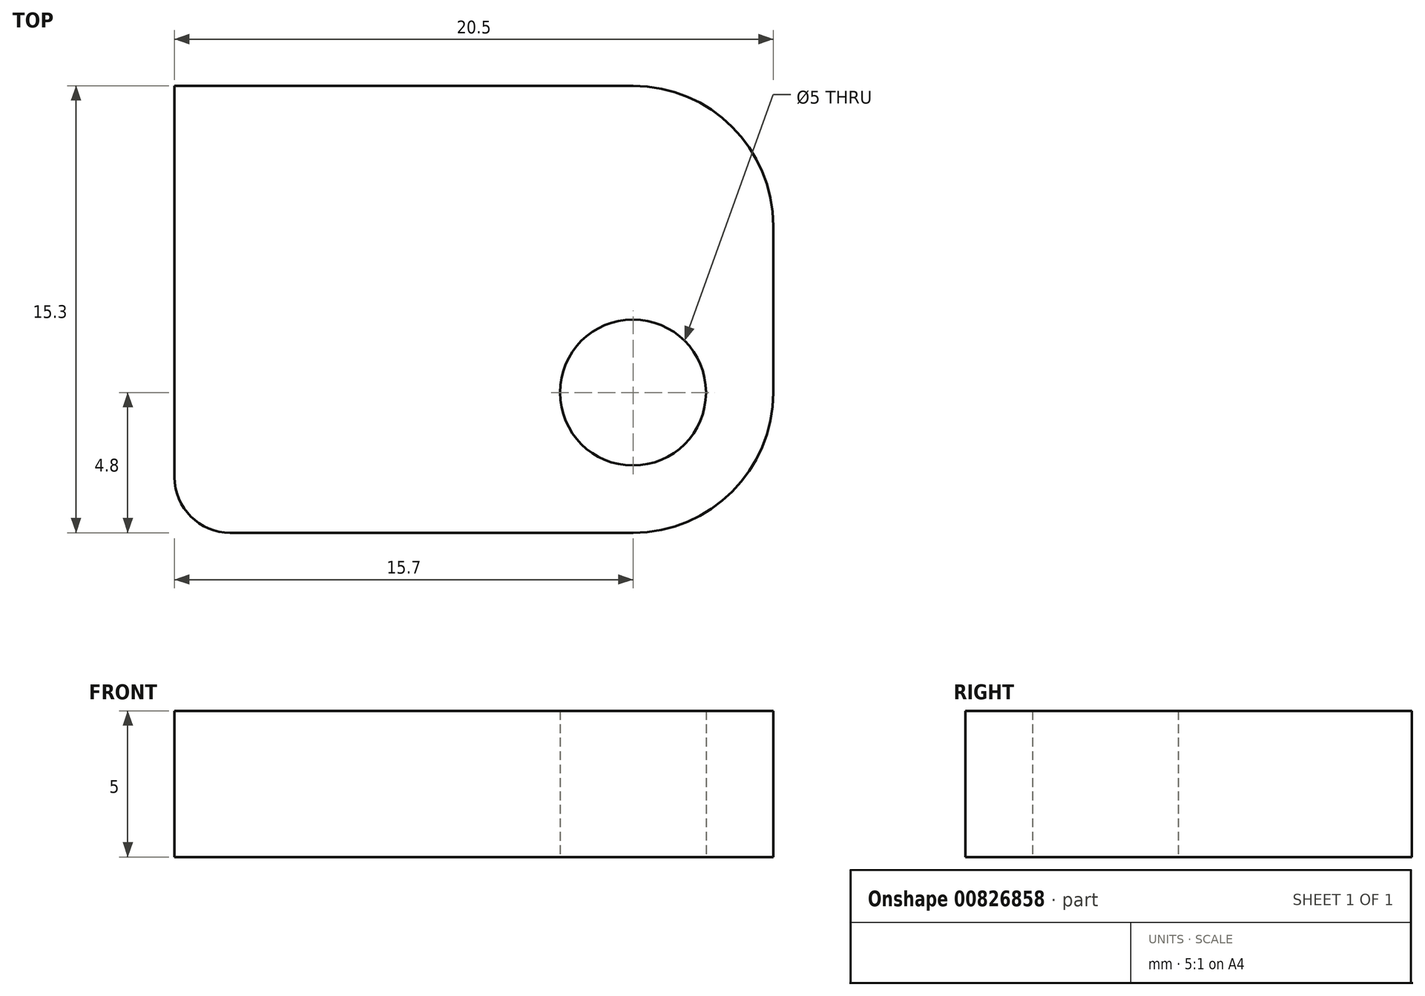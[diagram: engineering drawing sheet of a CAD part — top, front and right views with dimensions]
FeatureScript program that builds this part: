
annotation { "Feature Type Name" : "Feature", "Feature Type Description" : "" }
export const myFeature = defineFeature(function(context is Context, id is Id, definition is map)
    precondition{}
    {
        {
            var Q0;
            Q0=qCreatedBy(makeId("Top.planeOp"),FACE);
            var sketch = newSketch(context, id + "F0", { "sketchPlane" : qUnion([Q0])});
            skLineSegment(sketch, "E0.bottom", {"start": v(-10.25, 7.65) * mm, "end": v(5.45, 7.65) * mm});
            skLineSegment(sketch, "E0.top", {"start": v(-8.35, -7.65) * mm, "end": v(5.45, -7.65) * mm});
            skLineSegment(sketch, "E0.left", {"start": v(-10.25, 7.65) * mm, "end": v(-10.25, -5.75) * mm});
            skLineSegment(sketch, "E0.right", {"start": v(10.25, 2.85) * mm, "end": v(10.25, -2.85) * mm});
            skPoint(sketch, "E0.middle", {"position": v(0, 0) * mm});
            skPoint(sketch, "E1.visualSharp", {"position": v(10.25, 7.65) * mm});
            skArc(sketch, "E1.filletArc", {"start": v(10.25, 2.85) * mm, "mid": v(8.84, 6.24) * mm, "end": v(5.45, 7.65) * mm});
            skPoint(sketch, "E2.visualSharp", {"position": v(10.25, -7.65) * mm});
            skArc(sketch, "E2.filletArc", {"start": v(5.45, -7.65) * mm, "mid": v(8.84, -6.24) * mm, "end": v(10.25, -2.85) * mm});
            skPoint(sketch, "E3.visualSharp", {"position": v(-10.25, -7.65) * mm});
            skArc(sketch, "E3.filletArc", {"start": v(-10.25, -5.75) * mm, "mid": v(-9.7, -7.1) * mm, "end": v(-8.35, -7.65) * mm});
            skSolve(sketch);
        }
        {
            var Q0;
            Q0=makeQuery(id+"F0.imprint","IMPRINT",FACE,{"disambiguationData":[TD([[makeQuery(id+"F0.imprint","IMPRINT",EDGE,{"derivedFrom":sQuery(id+"F0.wireOp",EDGE,"E0.bottom")}),-1.0]])]});
            extrude(context, id + "F1", {"entities" : qUnion([Q0]), "depth" : 5 * mm, "offsetDistance" : 25 * mm});
        }
        {
            var Q0;
            Q0=sQuery(id+"F0.wireOp",VERTEX,"E2.filletArc.center");
            var Q1;
            Q1=makeQuery(id+"F1.opExtrude","SWEPT_BODY",BODY,{"disambiguationData":[OSD([sQuery(id+"F0.wireOp",EDGE,"E0.bottom"),sQuery(id+"F0.wireOp",EDGE,"E0.top"),sQuery(id+"F0.wireOp",EDGE,"E0.left"),sQuery(id+"F0.wireOp",EDGE,"E0.right"),sQuery(id+"F0.wireOp",EDGE,"E1.filletArc"),sQuery(id+"F0.wireOp",EDGE,"E2.filletArc")])]});
            hole(context, id + "F2", {"style" : HoleStyle.SIMPLE, "endStyle" : HoleEndStyle.THROUGH, "oppositeDirection" : true, "holeDiameter" : 5 * mm, "majorDiameter" : 5 * mm, "isTappedThrough" : true, "tappedDepth" : 12 * mm, "tapClearance" : 3, "locations" : qUnion([Q0]), "scope" : qUnion([Q1])});
        }
    });
